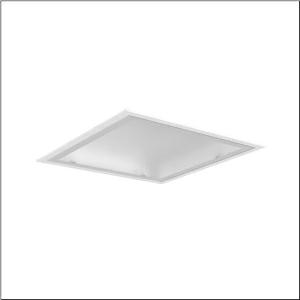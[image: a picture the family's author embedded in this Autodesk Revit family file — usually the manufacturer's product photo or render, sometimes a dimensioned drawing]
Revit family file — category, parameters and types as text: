
# Revit family: mira_11_51fr127a431a
name_source: partatom
category: Lighting Fixtures
units: mm (PartAtom-declared; Revit-internal decimal feet)

## family parameters
Cut with Voids When Loaded = No
Host = Face
Light Source = No
Part Type = Normal
Room Calculation Point = No
Round Connector Dimension = Use Diameter
Shared = No

## types (1)
- Mira 11 (1 x LED, 3060 lm, 23 W, 4000K)
    Apparent Load = 23 VA
    CIE Flux Codes = 51 82 97 100 100
    Color Rendering = 80
    Color Temperature = 4000K
    Default Elevation = 1800 mm
    Description = Mira 11, clean room luminaire, primary light control with reflector, primary optical cover: cover, of toughened safety glass, light emission: direct distribution, primary light characteristic: symmetric, installation type: recessed, LED, rated luminous flux: 3.060lm, luminous efficacy: 133lm/W, light colour: 840, colour temperature: 4000K, control gear: ON/OFF, with terminal, 3-pole, max. 2.5mm², mains connection: 230V, AC, 50/60Hz, rated input power: 23W, luminaire housing, of sheet steel, coated, pure white (RAL 9010), with concealed magnets, module: M625, length: 623mm, width: 623mm, height: 90mm, protection rating (complete): IP65, insulation class (complete): insulation class I (protective earthing), certification: CE, UKCA, permissible operating ambient temperature: -5..+40°C, standard: EN 50419, packaging unit: 1 piece
    Height = 0 mm  [stored 0 ft]
    Lamp = 1 x LED
    Lamp Light Flux = 3060 lm
    Lamp Power = 23 W
    Lamp count = 1
    Length = 625 mm
    Luminous efficacy = 133 lm/W
    Manufacturer = Siteco
    ModVariant = No
    Model = 51FR127A431A
    Mounting Place = Ceiling
    Mounting Type = Recessed
    Number of Poles = 1
    OnlyDefault = Yes
    Power Factor = 1
    Product Name = Mira 11
    Product group = clean room luminaire | ceiling recessed
    ProductGroupID = 402
    Protection Class = Protection class I
    Protection Degree = IP 65
    RLX_Detail_Level = 1
    RLX_Emergency_Light_Flux = 0 lm
    RLX_Emergency_Type = 0
    RLX_Emergency_Type_DB = No
    RlxData = <blob elided: 19277 chars, md5=bd07d2b1>
    Socket = socket
    Standby Power = 0 W
    System Light Flux = 3060 lm
    System Power = 23 W
    Type Comments = Product without accessories
    Type Image = l_1006636.jpg
    URL = http://relux.com
    VarID = ---
    Voltage = 0 V
    Weight = 0.00 kg
    Width = 625 mm

note: [stored X ft] marks values corroborated as IEEE doubles in the binary element streams (Revit-internal decimal feet)

## geometry (parser evidence)
native form markers: Blend x4, Sweep x9
no freeform markers — native parametric forms only
